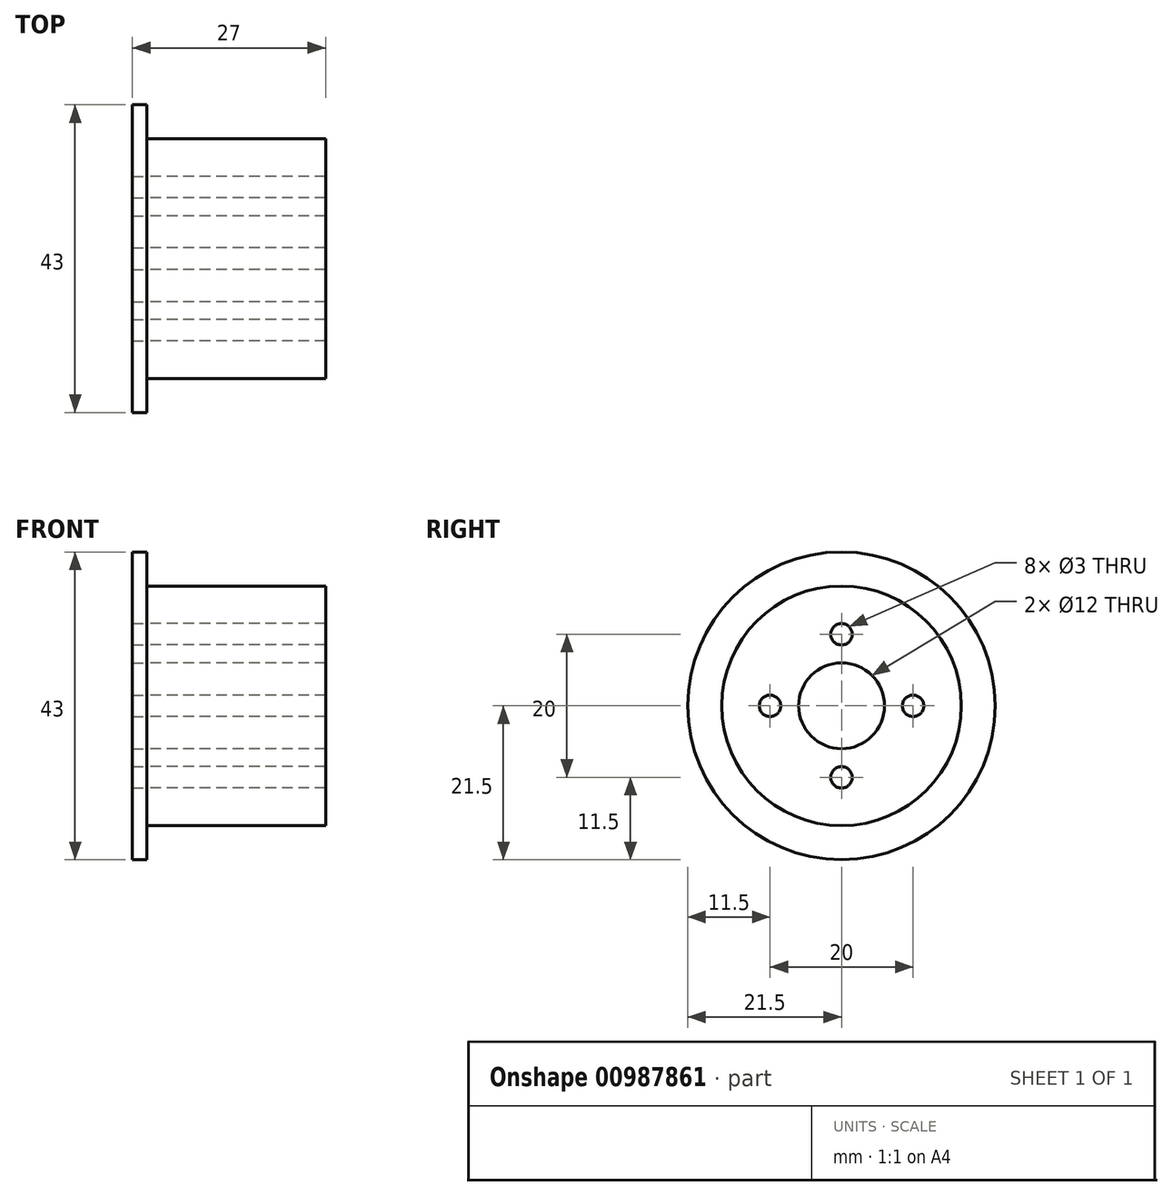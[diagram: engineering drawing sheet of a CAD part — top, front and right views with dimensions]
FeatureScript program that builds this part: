
annotation { "Feature Type Name" : "Feature", "Feature Type Description" : "" }
export const myFeature = defineFeature(function(context is Context, id is Id, definition is map)
    precondition{}
    {
        {
            var Q0;
            Q0=qCreatedBy(makeId("Right.planeOp"),FACE);
            var sketch = newSketch(context, id + "F0", { "sketchPlane" : qUnion([Q0])});
            skCircle(sketch, "E0", {"center": v(0, 0) * mm, "radius": 16.75 * mm});
            skCircle(sketch, "E1", {"center": v(0, 0) * mm, "radius": 6 * mm});
            skCircle(sketch, "E2", {"center": v(0, 0) * mm, "radius": 21.5 * mm});
            skCircle(sketch, "E3", {"center": v(0, 0) * mm, "radius": 10 * mm, "construction": true});
            skCircle(sketch, "E4", {"center": v(0, 10) * mm, "radius": 1.5 * mm});
            skCircle(sketch, "E5", {"center": v(-10, 0) * mm, "radius": 1.5 * mm});
            skCircle(sketch, "E6", {"center": v(0, -10) * mm, "radius": 1.5 * mm});
            skCircle(sketch, "E7", {"center": v(10, 0) * mm, "radius": 1.5 * mm});
            skSolve(sketch);
        }
        {
            var Q0;
            Q0=makeQuery(id+"F0.imprint","IMPRINT",FACE,{"disambiguationData":[TD([[makeQuery(id+"F0.imprint","IMPRINT",EDGE,{"derivedFrom":sQuery(id+"F0.wireOp",EDGE,"E0")}),1.0]])]});
            var Q1;
            Q1 = qBodyType(qCreatedBy(id + "F0" ,EDGE), BodyType.WIRE);
            var Q2;
            Q2=sQuery(id+"F0.wireOp",EDGE,"E0");
            extrude(context, id + "F1", {"entities" : qUnion([Q0]), "surfaceEntities" : qUnion([Q1, Q2]), "depth" : 25 * mm, "offsetDistance" : 25 * mm});
        }
        {
            var Q0;
            Q0=makeQuery(id+"F0.imprint","IMPRINT",FACE,{"disambiguationData":[TD([[makeQuery(id+"F0.imprint","IMPRINT",EDGE,{"derivedFrom":sQuery(id+"F0.wireOp",EDGE,"E0")}),-1.0]])]});
            var Q1;
            Q1=makeQuery(id+"F0.imprint","IMPRINT",FACE,{"disambiguationData":[TD([[makeQuery(id+"F0.imprint","IMPRINT",EDGE,{"derivedFrom":sQuery(id+"F0.wireOp",EDGE,"E0")}),1.0]])]});
            extrude(context, id + "F2", {"entities" : qUnion([Q0, Q1]), "oppositeDirection" : true, "depth" : 2 * mm, "offsetDistance" : 25 * mm});
        }
    });
